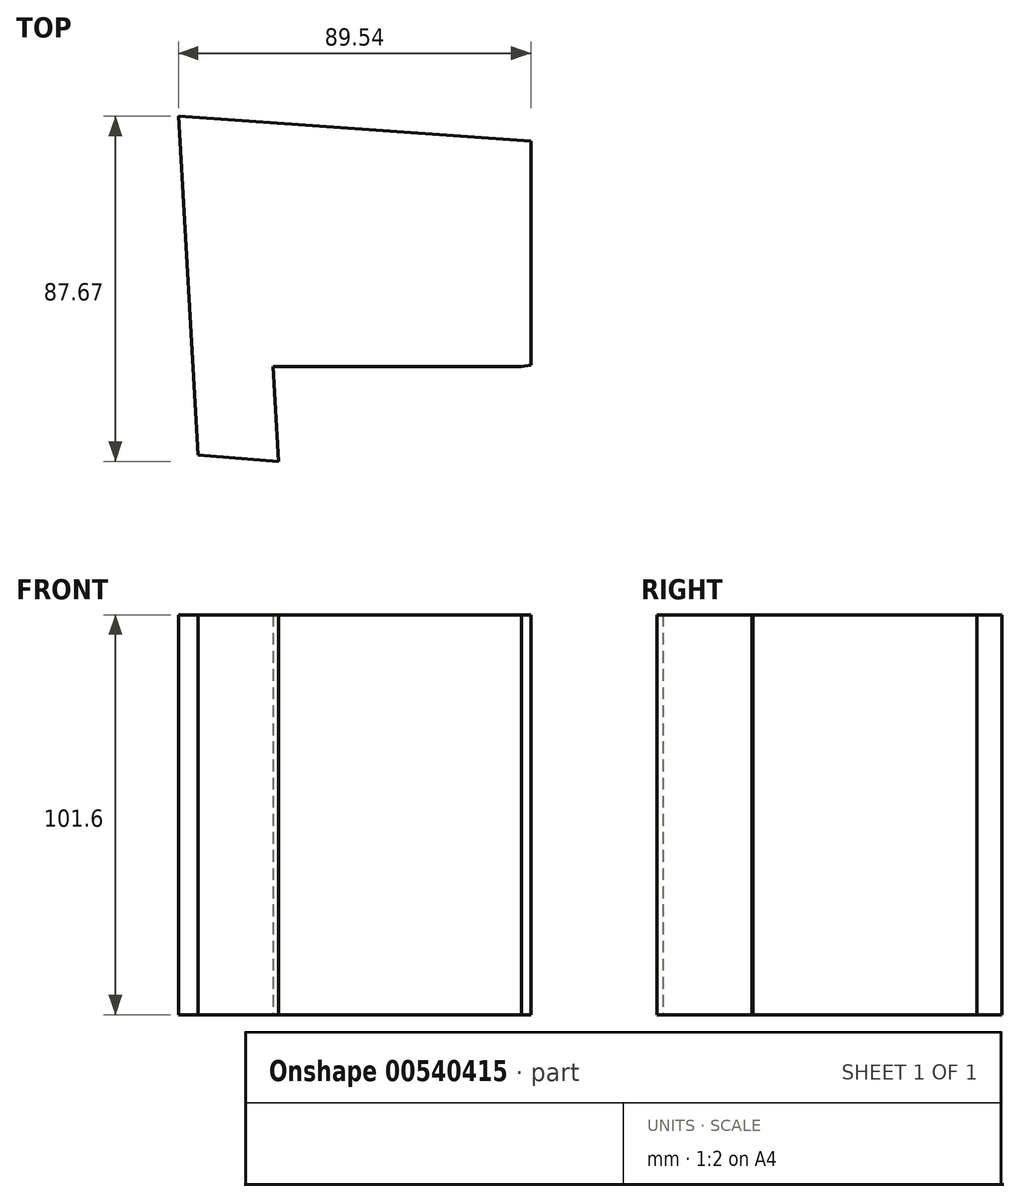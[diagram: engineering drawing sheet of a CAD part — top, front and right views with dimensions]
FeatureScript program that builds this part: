
annotation { "Feature Type Name" : "Feature", "Feature Type Description" : "" }
export const myFeature = defineFeature(function(context is Context, id is Id, definition is map)
    precondition{}
    {
        {
            var Q0;
            Q0=qCreatedBy(makeId("Top.planeOp"),FACE);
            var sketch = newSketch(context, id + "F0", { "sketchPlane" : qUnion([Q0])});
            skLineSegment(sketch, "E0", {"start": v(-112.53, -60.43) * mm, "end": v(-117.56, 25.71) * mm});
            skLineSegment(sketch, "E1", {"start": v(-117.56, 25.71) * mm, "end": v(-28.02, 19.43) * mm});
            skLineSegment(sketch, "E2", {"start": v(-28.02, 19.43) * mm, "end": v(-28.02, -37.49) * mm});
            skLineSegment(sketch, "E3", {"start": v(-28.02, -37.49) * mm, "end": v(-30.39, -37.83) * mm});
            skLineSegment(sketch, "E4", {"start": v(-30.39, -37.83) * mm, "end": v(-93.5, -37.83) * mm});
            skLineSegment(sketch, "E5", {"start": v(-93.5, -37.83) * mm, "end": v(-92.08, -61.96) * mm});
            skLineSegment(sketch, "E6", {"start": v(-92.08, -61.96) * mm, "end": v(-112.53, -60.43) * mm});
            skSolve(sketch);
        }
        {
            var Q0;
            Q0=makeQuery(id+"F0.imprint","IMPRINT",FACE,{"disambiguationData":[TD([[makeQuery(id+"F0.imprint","IMPRINT",EDGE,{"derivedFrom":sQuery(id+"F0.wireOp",EDGE,"E0")}),-1.0]])]});
            extrude(context, id + "F1", {"entities" : qUnion([Q0]), "depth" : 101.6 * mm, "offsetDistance" : 25.4 * mm});
        }
    });
